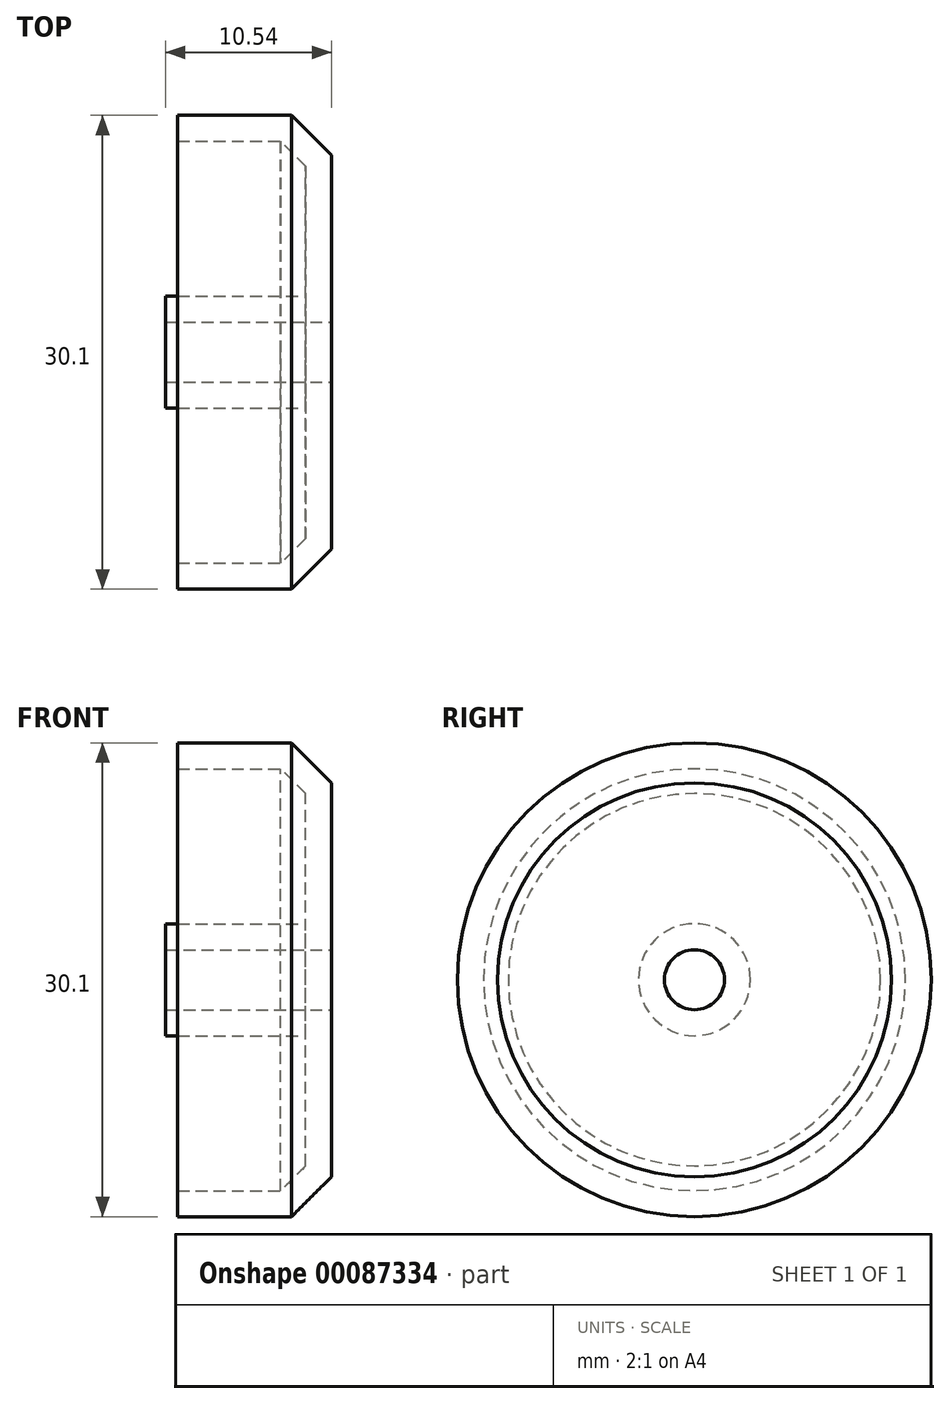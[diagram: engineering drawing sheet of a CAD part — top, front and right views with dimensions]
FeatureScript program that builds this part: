
annotation { "Feature Type Name" : "Feature", "Feature Type Description" : "" }
export const myFeature = defineFeature(function(context is Context, id is Id, definition is map)
    precondition{}
    {
        {
            var Q0;
            Q0=qCreatedBy(makeId("Front.planeOp"),FACE);
            var sketch = newSketch(context, id + "F0", { "sketchPlane" : qUnion([Q0])});
            skLineSegment(sketch, "E0", {"start": v(0.76, 15.05) * mm, "end": v(8, 15.05) * mm});
            skLineSegment(sketch, "E1", {"start": v(8, 15.05) * mm, "end": v(10.54, 12.5) * mm});
            skLineSegment(sketch, "E2", {"start": v(10.54, 12.5) * mm, "end": v(10.54, 0) * mm});
            skLineSegment(sketch, "E3", {"start": v(10.54, 0) * mm, "end": v(0, 0) * mm});
            skLineSegment(sketch, "E4.0", {"start": v(8.89, 3.56) * mm, "end": v(0, 3.56) * mm});
            skLineSegment(sketch, "E4.1", {"start": v(8.89, 11.83) * mm, "end": v(8.89, 3.56) * mm});
            skLineSegment(sketch, "E4.2", {"start": v(7.32, 13.4) * mm, "end": v(8.89, 11.83) * mm});
            skLineSegment(sketch, "E5", {"start": v(7.32, 13.4) * mm, "end": v(0.76, 13.4) * mm});
            skLineSegment(sketch, "E6", {"start": v(0.76, 13.4) * mm, "end": v(0.76, 15.05) * mm});
            skLineSegment(sketch, "E7", {"start": v(0, 3.56) * mm, "end": v(0, 0) * mm});
            skSolve(sketch);
        }
        {
            var Q0;
            Q0=makeQuery(id+"F0.imprint","IMPRINT",FACE,{"disambiguationData":[TD([[makeQuery(id+"F0.imprint","IMPRINT",EDGE,{"derivedFrom":sQuery(id+"F0.wireOp",EDGE,"xKeI8UTU-GpRI-q9U3-3FMW-edJCSYkuSLwx")}),-1.0]])]});
            var Q1;
            Q1=makeQuery(id+"F0.imprint","IMPRINT",FACE,{"disambiguationData":[TD([[makeQuery(id+"F0.imprint","IMPRINT",EDGE,{"derivedFrom":sQuery(id+"F0.wireOp",EDGE,"E0")}),-1.0]])]});
            var Q2;
            Q2=sQuery(id+"F0.wireOp",EDGE,"E3");
            revolve(context, id + "F1", {"entities" : qUnion([Q0, Q1]), "axis" : qUnion([Q2]), "revolveType" : RevolveType.FULL});
        }
        {
            var Q0;
            Q0=makeQuery(id+"F1.opRevolve","SWEPT_FACE",FACE,{"disambiguationData":[OSD([sQuery(id+"F0.wireOp",EDGE,"E2")])]});
            var sketch = newSketch(context, id + "F2", { "sketchPlane" : qUnion([Q0])});
            skCircle(sketch, "E8", {"center": v(0, 0) * mm, "radius": 1.9 * mm});
            skSolve(sketch);
        }
        {
            var Q0;
            Q0=makeQuery(id+"F2.imprint","IMPRINT",FACE,{"disambiguationData":[TD([[makeQuery(id+"F2.imprint","IMPRINT",EDGE,{"derivedFrom":sQuery(id+"F2.wireOp",EDGE,"E8")}),1.0]])]});
            extrude(context, id + "F3", {"entities" : qUnion([Q0]), "operationType" : NewBodyOperationType.REMOVE, "endBound" : BoundingType.THROUGH_ALL, "oppositeDirection" : true, "depth" : 3.17 * mm});
        }
    });
